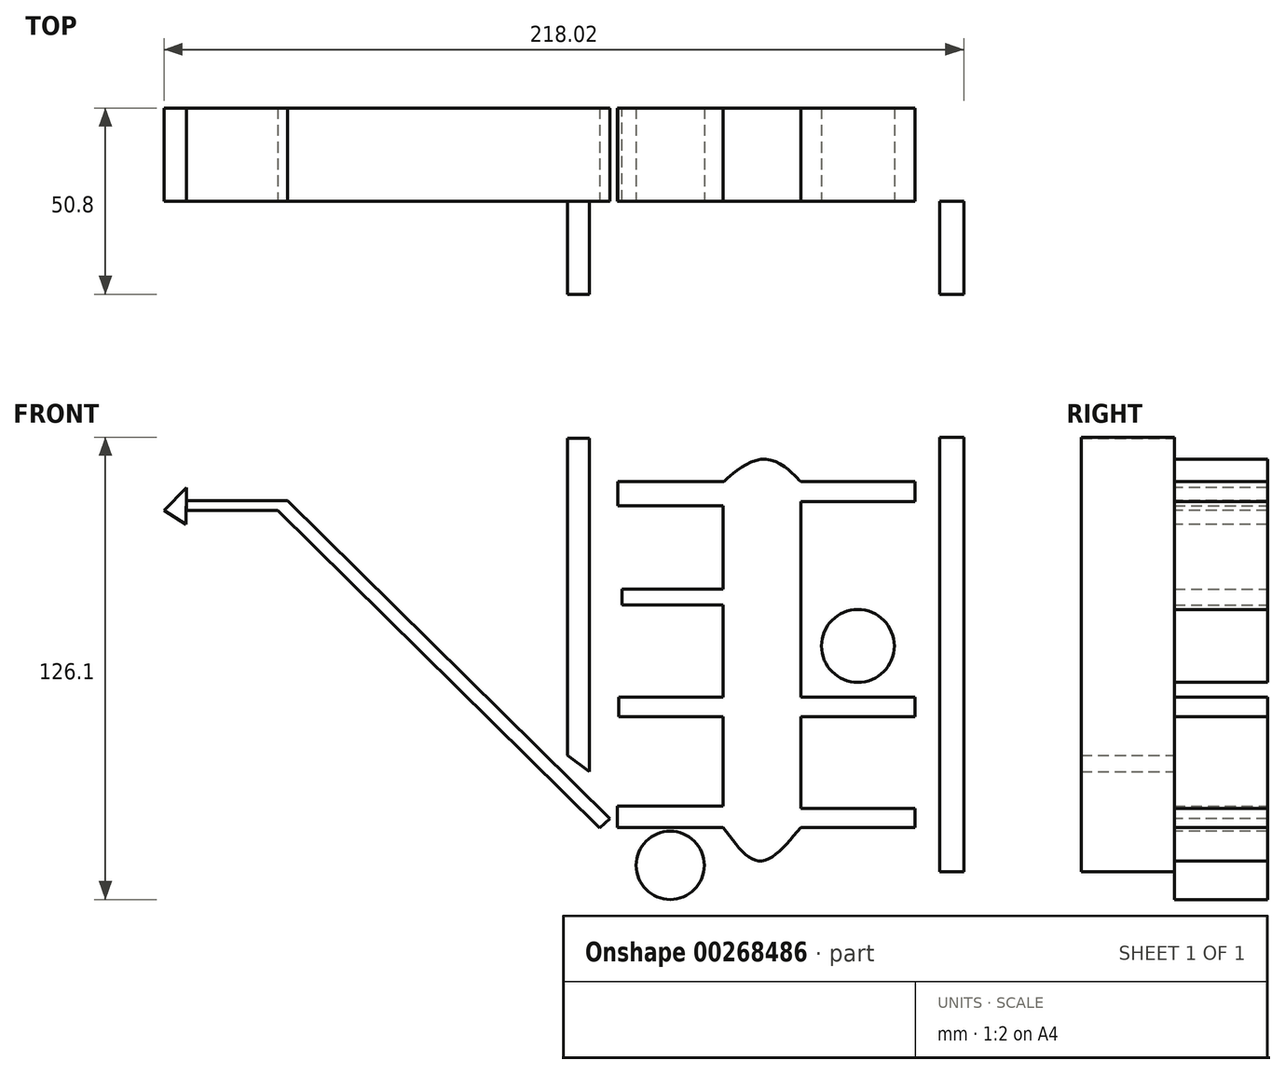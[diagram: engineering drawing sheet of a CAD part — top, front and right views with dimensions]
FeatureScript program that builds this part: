
annotation { "Feature Type Name" : "Feature", "Feature Type Description" : "" }
export const myFeature = defineFeature(function(context is Context, id is Id, definition is map)
    precondition{}
    {
        {
            var Q0;
            Q0=qCreatedBy(makeId("Front.planeOp"),FACE);
            var sketch = newSketch(context, id + "F0", { "sketchPlane" : qUnion([Q0])});
            skLineSegment(sketch, "E0", {"start": v(25.58, 29.22) * mm, "end": v(-5.6, 29.22) * mm});
            skLineSegment(sketch, "E1", {"start": v(-5.6, 29.22) * mm, "end": v(25.58, 29.22) * mm});
            skLineSegment(sketch, "E2", {"start": v(25.58, 24.93) * mm, "end": v(25.58, 29.22) * mm});
            skLineSegment(sketch, "E3", {"start": v(-5.6, 29.22) * mm, "end": v(-5.6, 24.93) * mm});
            skLineSegment(sketch, "E4", {"start": v(-5.6, 24.93) * mm, "end": v(25.58, 24.93) * mm});
            skLineSegment(sketch, "E5", {"start": v(-5.6, 53.3) * mm, "end": v(-5.6, 29.22) * mm});
            skLineSegment(sketch, "E6", {"start": v(-5.6, 24.93) * mm, "end": v(-5.6, 0) * mm});
            skLineSegment(sketch, "E7", {"start": v(-5.6, 0) * mm, "end": v(25.58, 0) * mm});
            skLineSegment(sketch, "E8", {"start": v(25.58, 0) * mm, "end": v(25.58, -5.32) * mm});
            skLineSegment(sketch, "E9", {"start": v(25.58, -5.32) * mm, "end": v(-5.6, -5.32) * mm});
            skLineSegment(sketch, "E10", {"start": v(-5.6, -5.32) * mm, "end": v(-5.6, 0) * mm});
            skLineSegment(sketch, "E11", {"start": v(-5.6, -30.34) * mm, "end": v(-5.6, -5.32) * mm});
            skLineSegment(sketch, "E12", {"start": v(25.58, -30.34) * mm, "end": v(-5.6, -30.34) * mm});
            skLineSegment(sketch, "E13", {"start": v(25.58, -35.57) * mm, "end": v(25.58, -30.34) * mm});
            skLineSegment(sketch, "E14", {"start": v(-5.6, -35.57) * mm, "end": v(-5.6, -30.34) * mm});
            skLineSegment(sketch, "E15", {"start": v(25.58, -35.57) * mm, "end": v(-5.6, -35.57) * mm});
            skLineSegment(sketch, "E16", {"start": v(-5.6, 53.3) * mm, "end": v(25.58, 53.3) * mm});
            skLineSegment(sketch, "E17", {"start": v(25.58, 53.3) * mm, "end": v(25.58, 58.72) * mm});
            skLineSegment(sketch, "E18", {"start": v(25.58, 58.72) * mm, "end": v(-5.6, 58.72) * mm});
            skLineSegment(sketch, "E19", {"start": v(-5.6, 58.72) * mm, "end": v(-5.6, 53.3) * mm});
            skFitSpline(sketch, "E20", {"points": [v(-5.6, 58.72) * mm, v(-15.31, 64.89) * mm, v(-26.7, 58.72) * mm, v(-15.68, 66) * mm, v(-5.6, 58.72) * mm]});
            skLineSegment(sketch, "E21", {"start": v(-26.7, 58.72) * mm, "end": v(-26.7, -35.57) * mm});
            skLineSegment(sketch, "E22", {"start": v(-26.7, -35.57) * mm, "end": v(-55.64, -35.57) * mm});
            skLineSegment(sketch, "E23", {"start": v(-55.64, -35.57) * mm, "end": v(-55.64, -29.78) * mm});
            skLineSegment(sketch, "E24", {"start": v(-55.64, -29.78) * mm, "end": v(-26.7, -29.78) * mm});
            skLineSegment(sketch, "E25", {"start": v(-26.7, -29.78) * mm, "end": v(-26.7, -16.71) * mm});
            skLineSegment(sketch, "E26", {"start": v(-26.7, -5.32) * mm, "end": v(-55.27, -5.32) * mm});
            skLineSegment(sketch, "E27", {"start": v(-55.27, -5.32) * mm, "end": v(-55.27, 0) * mm});
            skLineSegment(sketch, "E28", {"start": v(-55.27, 0) * mm, "end": v(-26.7, 0) * mm});
            skLineSegment(sketch, "E29", {"start": v(-26.7, 0) * mm, "end": v(-26.7, 25.11) * mm});
            skLineSegment(sketch, "E30", {"start": v(-26.7, 25.11) * mm, "end": v(-54.34, 25.11) * mm});
            skLineSegment(sketch, "E31", {"start": v(-54.34, 25.11) * mm, "end": v(-54.34, 29.4) * mm});
            skLineSegment(sketch, "E32", {"start": v(-54.34, 29.4) * mm, "end": v(-26.7, 29.4) * mm});
            skLineSegment(sketch, "E33", {"start": v(-26.7, 29.4) * mm, "end": v(-26.7, 58.72) * mm});
            skLineSegment(sketch, "E34", {"start": v(-55.46, 58.72) * mm, "end": v(-55.46, 52.19) * mm});
            skLineSegment(sketch, "E35", {"start": v(-55.46, 52.19) * mm, "end": v(-26.7, 52.19) * mm});
            skLineSegment(sketch, "E36", {"start": v(-26.7, 52.19) * mm, "end": v(-26.7, 58.72) * mm});
            skLineSegment(sketch, "E37", {"start": v(-55.46, 58.72) * mm, "end": v(-26.7, 58.72) * mm});
            skFitSpline(sketch, "E38", {"points": [v(-26.7, -35.57) * mm, v(-16.8, -44.72) * mm, v(-5.6, -35.57) * mm], "startDerivative": vector(19.69, -27.62) * mm, "endDerivative": vector(22.5, 27.3) * mm});
            skSolve(sketch);
        }
        {
            var Q0;
            Q0=makeQuery(id+"F0.imprint","IMPRINT",FACE,{"disambiguationData":[TD([[makeQuery(id+"F0.imprint","IMPRINT",EDGE,{"derivedFrom":sQuery(id+"F0.wireOp",EDGE,"E16")}),1.0]])]});
            var Q1;
            Q1=makeQuery(id+"F0.imprint","IMPRINT",FACE,{"disambiguationData":[TD([[makeQuery(id+"F0.imprint","IMPRINT",EDGE,{"derivedFrom":sQuery(id+"F0.wireOp",EDGE,"E3")}),-1.0]])]});
            var Q2;
            Q2=makeQuery(id+"F0.imprint","IMPRINT",FACE,{"disambiguationData":[TD([[makeQuery(id+"F0.imprint","IMPRINT",EDGE,{"derivedFrom":sQuery(id+"F0.wireOp",EDGE,"E34")}),1.0]])]});
            var Q3;
            {var subQ2=sQuery(id+"F0.wireOp",EDGE,"E30");Q3=makeQuery(id+"F0.imprint","IMPRINT",FACE,{"disambiguationData":[TD([[makeQuery(id+"F0.imprint","IMPRINT",EDGE,{"derivedFrom":subQ2}),-1.0]])]});}
            var Q4;
            Q4=makeQuery(id+"F0.imprint","IMPRINT",FACE,{"disambiguationData":[TD([[makeQuery(id+"F0.imprint","IMPRINT",EDGE,{"derivedFrom":sQuery(id+"F0.wireOp",EDGE,"E1")}),-1.0]])]});
            var Q5;
            Q5=makeQuery(id+"F0.imprint","IMPRINT",FACE,{"disambiguationData":[TD([[makeQuery(id+"F0.imprint","IMPRINT",EDGE,{"derivedFrom":sQuery(id+"F0.wireOp",EDGE,"E7")}),-1.0]])]});
            var Q6;
            {var subQ0=sQuery(id+"F0.wireOp",EDGE,"E26");Q6=makeQuery(id+"F0.imprint","IMPRINT",FACE,{"disambiguationData":[TD([[makeQuery(id+"F0.imprint","IMPRINT",EDGE,{"derivedFrom":subQ0}),-1.0]])]});}
            var Q7;
            {var subQ0=sQuery(id+"F0.wireOp",EDGE,"E22");Q7=makeQuery(id+"F0.imprint","IMPRINT",FACE,{"disambiguationData":[TD([[makeQuery(id+"F0.imprint","IMPRINT",EDGE,{"derivedFrom":subQ0}),-1.0]])]});}
            var Q8;
            Q8=makeQuery(id+"F0.imprint","IMPRINT",FACE,{"disambiguationData":[TD([[makeQuery(id+"F0.imprint","IMPRINT",EDGE,{"derivedFrom":sQuery(id+"F0.wireOp",EDGE,"E12")}),1.0]])]});
            extrude(context, id + "F1", {"entities" : qUnion([Q0, Q1, Q2, Q3, Q4, Q5, Q6, Q7, Q8]), "depth" : 25.4 * mm});
        }
        {
            var Q0;
            Q0=makeQuery(id+"F1.opExtrude","CAP_FACE",FACE,{"disambiguationData":[OSD([sQuery(id+"F0.wireOp",EDGE,"E1"),sQuery(id+"F0.wireOp",EDGE,"E2"),sQuery(id+"F0.wireOp",EDGE,"E4"),sQuery(id+"F0.wireOp",EDGE,"E5"),sQuery(id+"F0.wireOp",EDGE,"E6"),sQuery(id+"F0.wireOp",EDGE,"E7"),sQuery(id+"F0.wireOp",EDGE,"E8"),sQuery(id+"F0.wireOp",EDGE,"E9"),sQuery(id+"F0.wireOp",EDGE,"E11"),sQuery(id+"F0.wireOp",EDGE,"E12"),sQuery(id+"F0.wireOp",EDGE,"E13"),sQuery(id+"F0.wireOp",EDGE,"E15"),sQuery(id+"F0.wireOp",EDGE,"E16"),sQuery(id+"F0.wireOp",EDGE,"E17"),sQuery(id+"F0.wireOp",EDGE,"E18"),sQuery(id+"F0.wireOp",EDGE,"E20"),sQuery(id+"F0.wireOp",EDGE,"E21"),sQuery(id+"F0.wireOp",EDGE,"E22"),sQuery(id+"F0.wireOp",EDGE,"E23"),sQuery(id+"F0.wireOp",EDGE,"E24"),sQuery(id+"F0.wireOp",EDGE,"E25"),sQuery(id+"F0.wireOp",EDGE,"E26"),sQuery(id+"F0.wireOp",EDGE,"E27"),sQuery(id+"F0.wireOp",EDGE,"E28"),sQuery(id+"F0.wireOp",EDGE,"E29"),sQuery(id+"F0.wireOp",EDGE,"E30"),sQuery(id+"F0.wireOp",EDGE,"E31"),sQuery(id+"F0.wireOp",EDGE,"E32"),sQuery(id+"F0.wireOp",EDGE,"E33"),sQuery(id+"F0.wireOp",EDGE,"E34"),sQuery(id+"F0.wireOp",EDGE,"E35"),sQuery(id+"F0.wireOp",EDGE,"E37"),sQuery(id+"F0.wireOp",EDGE,"E38")])],"isStart":false});
            var sketch = newSketch(context, id + "F2", { "sketchPlane" : qUnion([Q0])});
            skCircle(sketch, "E39", {"center": v(9.99, 13.92) * mm, "radius": 9.94 * mm});
            skPoint(sketch, "E39.centerSnap0", {"position": v(9.99, 24.93) * mm});
            skCircle(sketch, "E40", {"center": v(-41.17, -45.92) * mm, "radius": 9.3 * mm});
            skPoint(sketch, "E40.centerSnap0", {"position": v(-41.17, -35.57) * mm});
            skLineSegment(sketch, "E41", {"start": v(-57.6, -33.15) * mm, "end": v(-145.52, 53.59) * mm});
            skLineSegment(sketch, "E42", {"start": v(-145.52, 53.59) * mm, "end": v(-148.2, 50.88) * mm});
            skLineSegment(sketch, "E43", {"start": v(-148.2, 50.88) * mm, "end": v(-60.35, -35.78) * mm});
            skLineSegment(sketch, "E44", {"start": v(-60.35, -35.78) * mm, "end": v(-57.6, -33.15) * mm});
            skLineSegment(sketch, "E45", {"start": v(-173.16, 50.88) * mm, "end": v(-148.2, 50.88) * mm});
            skLineSegment(sketch, "E46", {"start": v(-145.52, 53.59) * mm, "end": v(-173.04, 53.59) * mm});
            skLineSegment(sketch, "E47", {"start": v(-173.04, 53.59) * mm, "end": v(-173.16, 47.11) * mm});
            skLineSegment(sketch, "E48", {"start": v(-173.16, 47.11) * mm, "end": v(-173.04, 57.1) * mm});
            skLineSegment(sketch, "E49", {"start": v(-173.04, 57.1) * mm, "end": v(-179.17, 50.88) * mm});
            skLineSegment(sketch, "E50", {"start": v(-179.17, 50.88) * mm, "end": v(-173.16, 47.11) * mm});
            skSolve(sketch);
        }
        {
            var Q0;
            Q0=makeQuery(id+"F2.imprint","IMPRINT",FACE,{"disambiguationData":[TD([[makeQuery(id+"F2.imprint","IMPRINT",EDGE,{"derivedFrom":sQuery(id+"F2.wireOp",EDGE,"E39")}),1.0]])]});
            var Q1;
            Q1=makeQuery(id+"F2.imprint","IMPRINT",FACE,{"disambiguationData":[TD([[makeQuery(id+"F2.imprint","IMPRINT",EDGE,{"derivedFrom":sQuery(id+"F2.wireOp",EDGE,"E40")}),1.0]])]});
            var Q2;
            Q2=makeQuery(id+"F2.imprint","IMPRINT",FACE,{"disambiguationData":[TD([[makeQuery(id+"F2.imprint","IMPRINT",EDGE,{"derivedFrom":sQuery(id+"F2.wireOp",EDGE,"E41")}),1.0]])]});
            var Q3;
            {var subQ0=sQuery(id+"F2.wireOp",EDGE,"E42");Q3=makeQuery(id+"F2.imprint","IMPRINT",FACE,{"disambiguationData":[TD([[makeQuery(id+"F2.imprint","IMPRINT",EDGE,{"derivedFrom":subQ0}),-1.0]])]});}
            var Q4;
            {var subQ3=sQuery(id+"F2.wireOp",EDGE,"E49");Q4=makeQuery(id+"F2.imprint","IMPRINT",FACE,{"disambiguationData":[TD([[makeQuery(id+"F2.imprint","IMPRINT",EDGE,{"derivedFrom":subQ3}),1.0]])]});}
            extrude(context, id + "F3", {"entities" : qUnion([Q0, Q1, Q2, Q3, Q4]), "oppositeDirection" : true, "depth" : 25.4 * mm});
        }
        {
            var Q0;
            Q0=makeQuery(id+"F1.opExtrude","CAP_FACE",FACE,{"disambiguationData":[OSD([sQuery(id+"F0.wireOp",EDGE,"E1"),sQuery(id+"F0.wireOp",EDGE,"E2"),sQuery(id+"F0.wireOp",EDGE,"E4"),sQuery(id+"F0.wireOp",EDGE,"E5"),sQuery(id+"F0.wireOp",EDGE,"E6"),sQuery(id+"F0.wireOp",EDGE,"E7"),sQuery(id+"F0.wireOp",EDGE,"E8"),sQuery(id+"F0.wireOp",EDGE,"E9"),sQuery(id+"F0.wireOp",EDGE,"E11"),sQuery(id+"F0.wireOp",EDGE,"E12"),sQuery(id+"F0.wireOp",EDGE,"E13"),sQuery(id+"F0.wireOp",EDGE,"E15"),sQuery(id+"F0.wireOp",EDGE,"E16"),sQuery(id+"F0.wireOp",EDGE,"E17"),sQuery(id+"F0.wireOp",EDGE,"E18"),sQuery(id+"F0.wireOp",EDGE,"E20"),sQuery(id+"F0.wireOp",EDGE,"E21"),sQuery(id+"F0.wireOp",EDGE,"E22"),sQuery(id+"F0.wireOp",EDGE,"E23"),sQuery(id+"F0.wireOp",EDGE,"E24"),sQuery(id+"F0.wireOp",EDGE,"E25"),sQuery(id+"F0.wireOp",EDGE,"E26"),sQuery(id+"F0.wireOp",EDGE,"E27"),sQuery(id+"F0.wireOp",EDGE,"E28"),sQuery(id+"F0.wireOp",EDGE,"E29"),sQuery(id+"F0.wireOp",EDGE,"E30"),sQuery(id+"F0.wireOp",EDGE,"E31"),sQuery(id+"F0.wireOp",EDGE,"E32"),sQuery(id+"F0.wireOp",EDGE,"E33"),sQuery(id+"F0.wireOp",EDGE,"E34"),sQuery(id+"F0.wireOp",EDGE,"E35"),sQuery(id+"F0.wireOp",EDGE,"E37"),sQuery(id+"F0.wireOp",EDGE,"E38")])],"isStart":false});
            var sketch = newSketch(context, id + "F4", { "sketchPlane" : qUnion([Q0])});
            skLineSegment(sketch, "E51", {"start": v(32.3, 63.14) * mm, "end": v(32.3, -47.64) * mm});
            skLineSegment(sketch, "E52", {"start": v(32.3, -47.64) * mm, "end": v(38.85, -47.64) * mm});
            skLineSegment(sketch, "E53", {"start": v(38.85, -47.64) * mm, "end": v(38.85, 62.97) * mm});
            skLineSegment(sketch, "E54", {"start": v(38.85, 62.97) * mm, "end": v(32.3, 63.14) * mm});
            skLineSegment(sketch, "E55", {"start": v(-63.26, 63.14) * mm, "end": v(-69.2, 63.14) * mm});
            skLineSegment(sketch, "E56", {"start": v(-69.2, 63.14) * mm, "end": v(-69.2, -15.96) * mm});
            skLineSegment(sketch, "E57", {"start": v(-69.2, -15.96) * mm, "end": v(-69.2, 63.14) * mm});
            skLineSegment(sketch, "E58", {"start": v(-63.26, 63.14) * mm, "end": v(-63.26, -20.37) * mm});
            skLineSegment(sketch, "E59", {"start": v(-63.26, -20.37) * mm, "end": v(-69.2, -15.96) * mm});
            skLineSegment(sketch, "E60", {"start": v(38.85, 62.97) * mm, "end": v(38.85, 70.87) * mm});
            skLineSegment(sketch, "E61", {"start": v(38.85, 70.87) * mm, "end": v(32.3, 70.87) * mm});
            skLineSegment(sketch, "E62", {"start": v(32.3, 70.87) * mm, "end": v(32.3, 63.14) * mm});
            skLineSegment(sketch, "E63", {"start": v(-63.26, 63.14) * mm, "end": v(-63.26, 70.55) * mm});
            skLineSegment(sketch, "E64", {"start": v(-63.26, 70.55) * mm, "end": v(-69.2, 70.55) * mm});
            skLineSegment(sketch, "E65", {"start": v(-69.2, 70.55) * mm, "end": v(-69.2, 63.14) * mm});
            skSolve(sketch);
        }
        {
            var Q0;
            Q0=makeQuery(id+"F4.imprint","IMPRINT",FACE,{"disambiguationData":[TD([[makeQuery(id+"F4.imprint","IMPRINT",EDGE,{"derivedFrom":sQuery(id+"F4.wireOp",EDGE,"E51")}),1.0]])]});
            var Q1;
            Q1=makeQuery(id+"F4.imprint","IMPRINT",FACE,{"disambiguationData":[TD([[makeQuery(id+"F4.imprint","IMPRINT",EDGE,{"derivedFrom":sQuery(id+"F4.wireOp",EDGE,"E54")}),-1.0]])]});
            var Q2;
            Q2=makeQuery(id+"F4.imprint","IMPRINT",FACE,{"disambiguationData":[TD([[makeQuery(id+"F4.imprint","IMPRINT",EDGE,{"derivedFrom":sQuery(id+"F4.wireOp",EDGE,"E55")}),-1.0]])]});
            var Q3;
            Q3=makeQuery(id+"F4.imprint","IMPRINT",FACE,{"disambiguationData":[TD([[makeQuery(id+"F4.imprint","IMPRINT",EDGE,{"derivedFrom":sQuery(id+"F4.wireOp",EDGE,"E55")}),1.0]])]});
            extrude(context, id + "F5", {"entities" : qUnion([Q0, Q1, Q2, Q3]), "depth" : 25.4 * mm});
        }
        {
            var Q0;
            Q0=makeQuery(id+"F1.opExtrude","CAP_FACE",FACE,{"disambiguationData":[OSD([sQuery(id+"F0.wireOp",EDGE,"E1"),sQuery(id+"F0.wireOp",EDGE,"E2"),sQuery(id+"F0.wireOp",EDGE,"E4"),sQuery(id+"F0.wireOp",EDGE,"E5"),sQuery(id+"F0.wireOp",EDGE,"E6"),sQuery(id+"F0.wireOp",EDGE,"E7"),sQuery(id+"F0.wireOp",EDGE,"E8"),sQuery(id+"F0.wireOp",EDGE,"E9"),sQuery(id+"F0.wireOp",EDGE,"E11"),sQuery(id+"F0.wireOp",EDGE,"E12"),sQuery(id+"F0.wireOp",EDGE,"E13"),sQuery(id+"F0.wireOp",EDGE,"E15"),sQuery(id+"F0.wireOp",EDGE,"E16"),sQuery(id+"F0.wireOp",EDGE,"E17"),sQuery(id+"F0.wireOp",EDGE,"E18"),sQuery(id+"F0.wireOp",EDGE,"E20"),sQuery(id+"F0.wireOp",EDGE,"E21"),sQuery(id+"F0.wireOp",EDGE,"E22"),sQuery(id+"F0.wireOp",EDGE,"E23"),sQuery(id+"F0.wireOp",EDGE,"E24"),sQuery(id+"F0.wireOp",EDGE,"E25"),sQuery(id+"F0.wireOp",EDGE,"E26"),sQuery(id+"F0.wireOp",EDGE,"E27"),sQuery(id+"F0.wireOp",EDGE,"E28"),sQuery(id+"F0.wireOp",EDGE,"E29"),sQuery(id+"F0.wireOp",EDGE,"E30"),sQuery(id+"F0.wireOp",EDGE,"E31"),sQuery(id+"F0.wireOp",EDGE,"E32"),sQuery(id+"F0.wireOp",EDGE,"E33"),sQuery(id+"F0.wireOp",EDGE,"E34"),sQuery(id+"F0.wireOp",EDGE,"E35"),sQuery(id+"F0.wireOp",EDGE,"E37"),sQuery(id+"F0.wireOp",EDGE,"E38")])],"isStart":false});
            var sketch = newSketch(context, id + "F6", { "sketchPlane" : qUnion([Q0])});
            skLineSegment(sketch, "E66", {"start": v(32.73, 70.19) * mm, "end": v(19.16, 81.83) * mm});
            skLineSegment(sketch, "E67", {"start": v(19.16, 81.83) * mm, "end": v(23.4, 86.77) * mm});
            skLineSegment(sketch, "E68", {"start": v(23.4, 86.77) * mm, "end": v(40.44, 72.13) * mm});
            skLineSegment(sketch, "E69", {"start": v(40.44, 69.33) * mm, "end": v(39.48, 70.15) * mm});
            skLineSegment(sketch, "E70", {"start": v(40.44, 72.13) * mm, "end": v(40.44, 69.33) * mm});
            skLineSegment(sketch, "E71", {"start": v(-68.56, 69.33) * mm, "end": v(-57.6, 91.12) * mm});
            skLineSegment(sketch, "E72", {"start": v(-63.05, 69.33) * mm, "end": v(-53.4, 83.5) * mm});
            skLineSegment(sketch, "E73", {"start": v(-57.6, 91.12) * mm, "end": v(-53.4, 83.5) * mm});
            skSolve(sketch);
        }
        {
            var Q0;
            Q0=sQuery(id+"F6.wireOp",EDGE,"E68");
            var Q1;
            Q1=sQuery(id+"F6.wireOp",EDGE,"E66");
            var Q2;
            Q2=sQuery(id+"F6.wireOp",EDGE,"E67");
            var Q3;
            Q3=sQuery(id+"F6.wireOp",EDGE,"E70");
            var Q4;
            Q4=sQuery(id+"F6.wireOp",EDGE,"E71");
            var Q5;
            Q5=sQuery(id+"F6.wireOp",EDGE,"E73");
            var Q6;
            Q6=sQuery(id+"F6.wireOp",EDGE,"E72");
            extrude(context, id + "F7", {"bodyType" : ToolBodyType.SURFACE, "surfaceEntities" : qUnion([Q0, Q1, Q2, Q3, Q4, Q5, Q6]), "oppositeDirection" : true, "depth" : 25.4 * mm});
        }
    });
